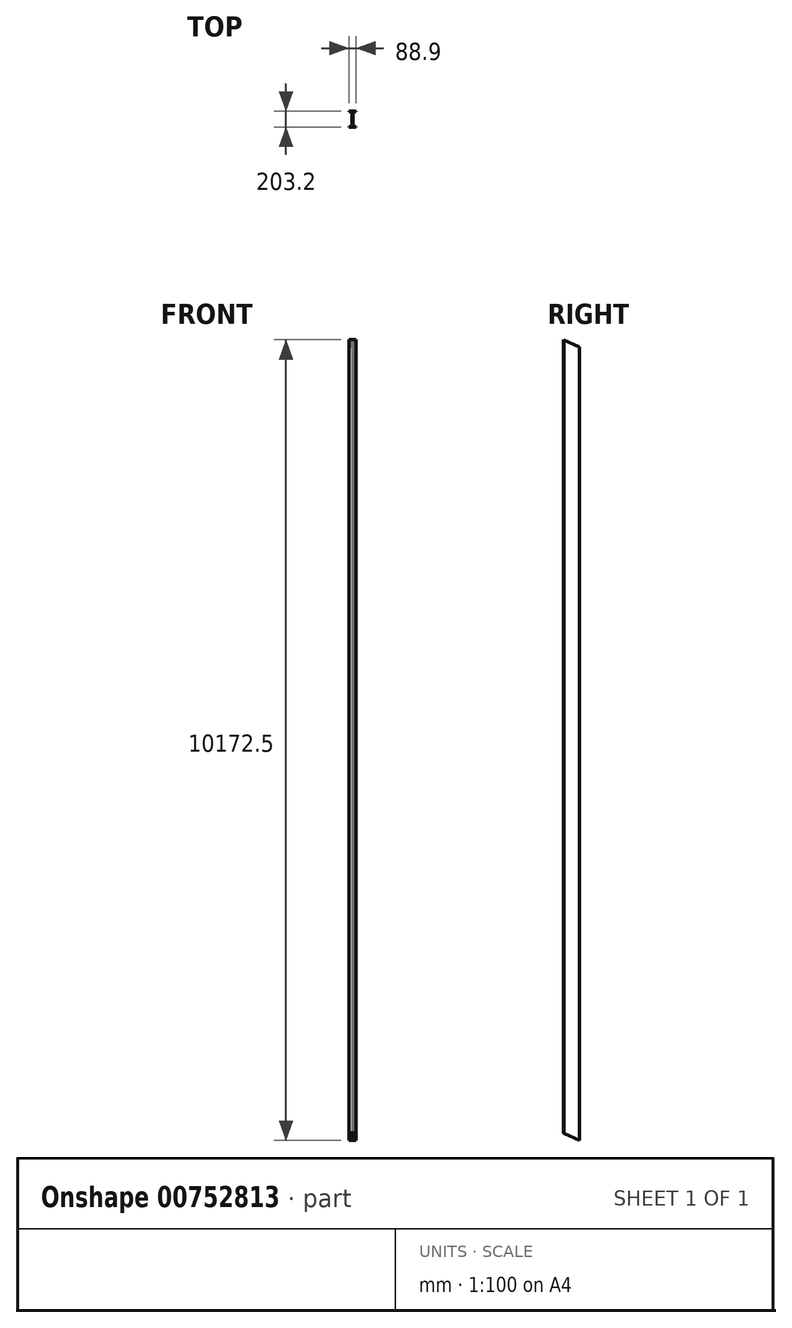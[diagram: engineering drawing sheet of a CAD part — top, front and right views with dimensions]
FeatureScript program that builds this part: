
annotation { "Feature Type Name" : "Feature", "Feature Type Description" : "" }
export const myFeature = defineFeature(function(context is Context, id is Id, definition is map)
    precondition{}
    {
        {
            var Q0;
            Q0=qCreatedBy(makeId("Top.planeOp"),FACE);
            var sketch = newSketch(context, id + "F0", { "sketchPlane" : qUnion([Q0])});
            skLineSegment(sketch, "E0.bottom", {"start": v(44.45, 101.6) * mm, "end": v(-44.45, 101.6) * mm});
            skLineSegment(sketch, "E0.top", {"start": v(44.45, -101.6) * mm, "end": v(-44.45, -101.6) * mm});
            skLineSegment(sketch, "E0.left", {"start": v(44.45, 101.6) * mm, "end": v(44.45, -101.6) * mm});
            skLineSegment(sketch, "E0.right", {"start": v(-44.45, 101.6) * mm, "end": v(-44.45, -101.6) * mm});
            skPoint(sketch, "E0.middle", {"position": v(0, 0) * mm});
            skSolve(sketch);
        }
        {
            var Q0;
            Q0=makeQuery(id+"F0.imprint","IMPRINT",FACE,{"disambiguationData":[TD([[makeQuery(id+"F0.imprint","IMPRINT",EDGE,{"derivedFrom":sQuery(id+"F0.wireOp",EDGE,"E0.bottom")}),1.0]])]});
            extrude(context, id + "F1", {"entities" : qUnion([Q0]), "depth" : 10668 * mm, "offsetDistance" : 25.4 * mm});
        }
        {
            var Q0;
            Q0=qCreatedBy(makeId("Top.planeOp"),FACE);
            var sketch = newSketch(context, id + "F2", { "sketchPlane" : qUnion([Q0])});
            skLineSegment(sketch, "E1.0.0", {"start": v(44.45, -101.6) * mm, "end": v(-44.45, -101.6) * mm, "construction": true});
            skLineSegment(sketch, "E1.0.1", {"start": v(-44.45, -101.6) * mm, "end": v(-44.45, 101.6) * mm, "construction": true});
            skLineSegment(sketch, "E1.0.2", {"start": v(-44.45, 101.6) * mm, "end": v(44.45, 101.6) * mm, "construction": true});
            skLineSegment(sketch, "E1.0.3", {"start": v(44.45, 101.6) * mm, "end": v(44.45, -101.6) * mm, "construction": true});
            skLineSegment(sketch, "E2.bottom", {"start": v(-44.45, -96.52) * mm, "end": v(-4.76, -96.52) * mm});
            skLineSegment(sketch, "E2.top", {"start": v(-44.45, 96.52) * mm, "end": v(-4.76, 96.52) * mm});
            skLineSegment(sketch, "E2.left", {"start": v(-44.45, -96.52) * mm, "end": v(-44.45, 96.52) * mm});
            skLineSegment(sketch, "E2.right", {"start": v(-4.76, -96.52) * mm, "end": v(-4.76, 96.52) * mm});
            skLineSegment(sketch, "E3.bottom", {"start": v(44.45, -96.52) * mm, "end": v(4.76, -96.52) * mm});
            skLineSegment(sketch, "E3.top", {"start": v(44.45, 96.52) * mm, "end": v(4.76, 96.52) * mm});
            skLineSegment(sketch, "E3.left", {"start": v(44.45, -96.52) * mm, "end": v(44.45, 96.52) * mm});
            skLineSegment(sketch, "E3.right", {"start": v(4.76, -96.52) * mm, "end": v(4.76, 96.52) * mm});
            skSolve(sketch);
        }
        {
            var Q0;
            Q0=makeQuery(id+"F2.imprint","IMPRINT",FACE,{"disambiguationData":[TD([[makeQuery(id+"F2.imprint","IMPRINT",EDGE,{"derivedFrom":sQuery(id+"F2.wireOp",EDGE,"E2.bottom")}),1.0]])]});
            var Q1;
            Q1=makeQuery(id+"F2.imprint","IMPRINT",FACE,{"disambiguationData":[TD([[makeQuery(id+"F2.imprint","IMPRINT",EDGE,{"derivedFrom":sQuery(id+"F2.wireOp",EDGE,"E3.bottom")}),-1.0]])]});
            extrude(context, id + "F3", {"entities" : qUnion([Q0, Q1]), "operationType" : NewBodyOperationType.REMOVE, "endBound" : BoundingType.THROUGH_ALL, "depth" : 25.4 * mm, "offsetDistance" : 25.4 * mm});
        }
        {
            var Q0;
            Q0=qCreatedBy(makeId("Right.planeOp"),FACE);
            var sketch = newSketch(context, id + "F4", { "sketchPlane" : qUnion([Q0])});
            skLineSegment(sketch, "E4.0", {"start": v(-96.52, 0) * mm, "end": v(96.52, 0) * mm, "construction": true});
            skLineSegment(sketch, "E5.0.1", {"start": v(101.6, 0) * mm, "end": v(101.6, 10668) * mm});
            skLineSegment(sketch, "E5.0.3", {"start": v(101.6, 10668) * mm, "end": v(101.6, 0) * mm});
            skLineSegment(sketch, "E6.0", {"start": v(-101.6, 10668) * mm, "end": v(-101.6, 0) * mm});
            skLineSegment(sketch, "E7", {"start": v(-101.6, 94.18) * mm, "end": v(4526.27, -2050.72) * mm});
            skLineSegment(sketch, "E8", {"start": v(-101.6, 94.18) * mm, "end": v(-101.6, 0) * mm});
            skLineSegment(sketch, "E9", {"start": v(-101.6, 0) * mm, "end": v(101.6, 0) * mm});
            skLineSegment(sketch, "E10", {"start": v(4526.27, -2050.72) * mm, "end": v(8371.38, 6245.53) * mm});
            skLineSegment(sketch, "E11", {"start": v(8371.38, 6245.53) * mm, "end": v(-101.6, 10172.55) * mm});
            skLineSegment(sketch, "E12", {"start": v(-101.6, 10172.55) * mm, "end": v(-101.6, 0) * mm});
            skSolve(sketch);
        }
        {
            var Q0;
            {var subQ3=sQuery(id+"F4.wireOp",EDGE,"E11");var subQ5=sQuery(id+"F4.wireOp",EDGE,"E12");var subQ7=makeQuery(id+"F4.imprint","INTERSECT",VERTEX,{"derivedFrom":[subQ3,subQ5]});Q0=makeQuery(id+"F4.imprint","IMPRINT",FACE,{"disambiguationData":[TD([[makeQuery(id+"F4.imprint","IMPRINT",EDGE,{"disambiguationData":[TD([[subQ7,1.0]])],"derivedFrom":subQ3}),1.0]])]});}
            extrude(context, id + "F5", {"entities" : qUnion([Q0]), "operationType" : NewBodyOperationType.INTERSECT, "depth" : 127 * mm, "offsetDistance" : 25.4 * mm, "symmetric" : true});
        }
    });
